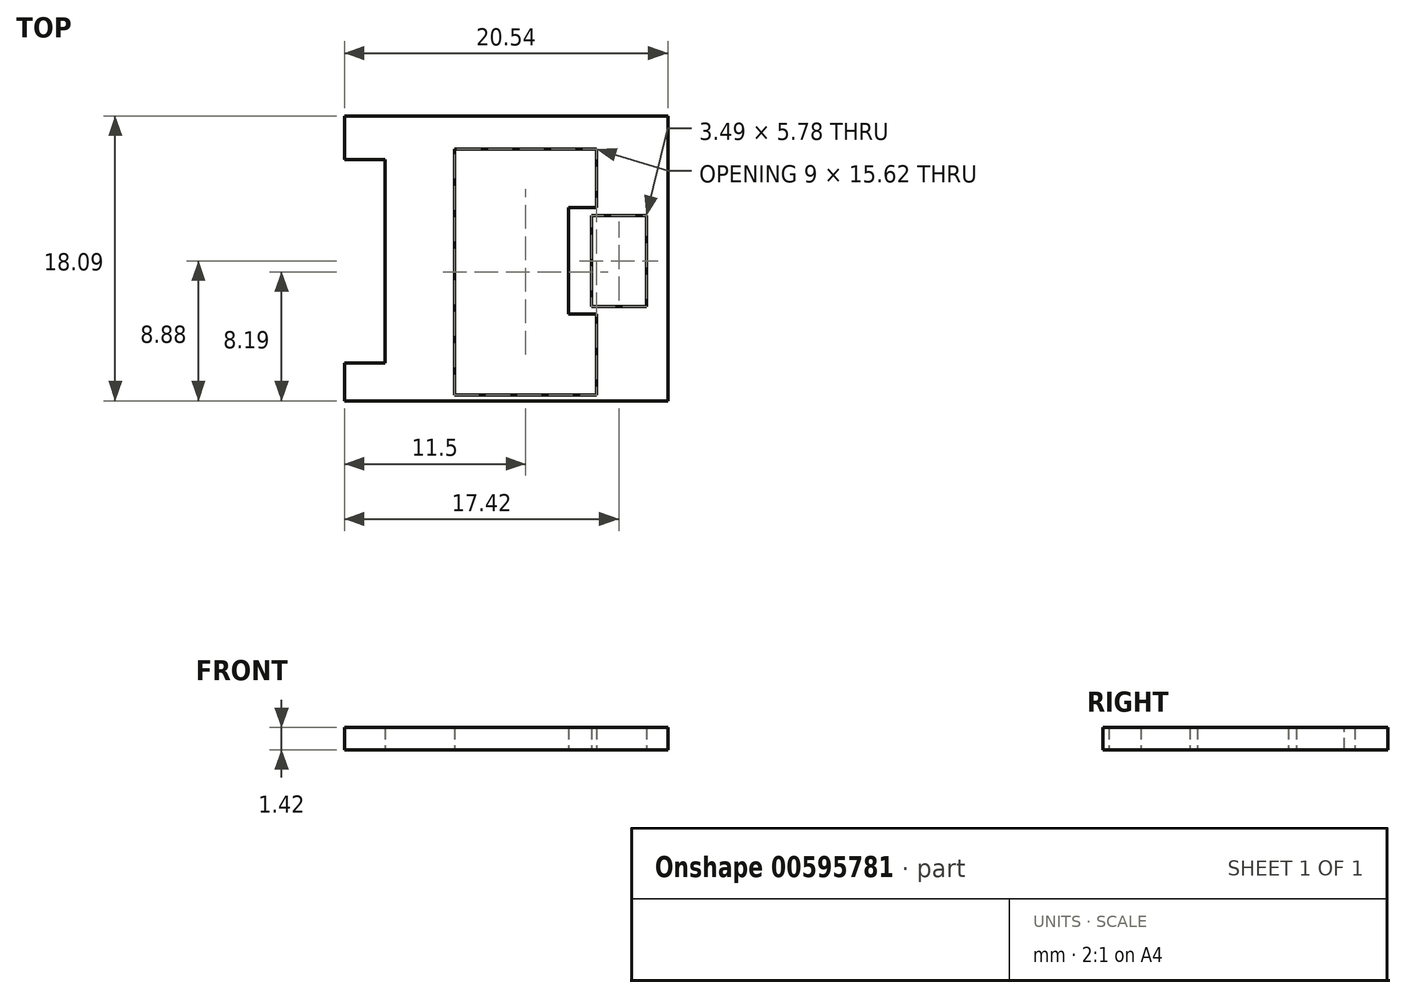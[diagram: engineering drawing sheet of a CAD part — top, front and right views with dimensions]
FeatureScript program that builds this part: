
annotation { "Feature Type Name" : "Feature", "Feature Type Description" : "" }
export const myFeature = defineFeature(function(context is Context, id is Id, definition is map)
    precondition{}
    {
        {
            var Q0;
            Q0=qCreatedBy(makeId("Top.planeOp"),FACE);
            var sketch = newSketch(context, id + "F0", { "sketchPlane" : qUnion([Q0])});
            skLineSegment(sketch, "E0.bottom", {"start": v(0, 0) * mm, "end": v(20.54, 0) * mm});
            skLineSegment(sketch, "E0.top", {"start": v(0, 18.1) * mm, "end": v(20.54, 18.1) * mm});
            skLineSegment(sketch, "E0.left", {"start": v(0, 0) * mm, "end": v(0, 18.1) * mm});
            skLineSegment(sketch, "E0.right", {"start": v(20.54, 0) * mm, "end": v(20.54, 18.1) * mm});
            skLineSegment(sketch, "E1.bottom", {"start": v(2.58, 15.3) * mm, "end": v(0.01, 15.3) * mm});
            skLineSegment(sketch, "E1.top", {"start": v(2.58, 2.4) * mm, "end": v(0.01, 2.4) * mm});
            skLineSegment(sketch, "E1.left", {"start": v(2.59, 15.3) * mm, "end": v(2.59, 2.4) * mm});
            skLineSegment(sketch, "E1.right", {"start": v(0.02, 15.3) * mm, "end": v(0.02, 2.4) * mm});
            skPoint(sketch, "E1.middle", {"position": v(1.3, 8.86) * mm});
            skLineSegment(sketch, "E2", {"start": v(7, 16) * mm, "end": v(16, 16) * mm});
            skLineSegment(sketch, "E3", {"start": v(16, 16) * mm, "end": v(16, 12.27) * mm});
            skLineSegment(sketch, "E4", {"start": v(16, 12.27) * mm, "end": v(14.23, 12.27) * mm});
            skLineSegment(sketch, "E5", {"start": v(14.23, 12.27) * mm, "end": v(14.23, 5.5) * mm});
            skLineSegment(sketch, "E6", {"start": v(14.23, 5.5) * mm, "end": v(16, 5.5) * mm});
            skLineSegment(sketch, "E7", {"start": v(16, 5.5) * mm, "end": v(16, 0.38) * mm});
            skLineSegment(sketch, "E8", {"start": v(16, 0.38) * mm, "end": v(7, 0.38) * mm});
            skLineSegment(sketch, "E9", {"start": v(7, 0.38) * mm, "end": v(7, 16) * mm});
            skLineSegment(sketch, "E10.bottom", {"start": v(19.17, 11.77) * mm, "end": v(15.68, 11.77) * mm});
            skLineSegment(sketch, "E10.top", {"start": v(19.17, 6) * mm, "end": v(15.68, 6) * mm});
            skLineSegment(sketch, "E10.left", {"start": v(19.17, 11.77) * mm, "end": v(19.17, 6) * mm});
            skLineSegment(sketch, "E10.right", {"start": v(15.68, 11.77) * mm, "end": v(15.68, 6) * mm});
            skPoint(sketch, "E10.middle", {"position": v(17.42, 8.88) * mm});
            skSolve(sketch);
        }
        {
            var Q0;
            Q0=makeQuery(id+"F0.imprint","IMPRINT",FACE,{"disambiguationData":[TD([[makeQuery(id+"F0.imprint","IMPRINT",EDGE,{"derivedFrom":sQuery(id+"F0.wireOp",EDGE,"E0.bottom")}),1.0]])]});
            extrude(context, id + "F1", {"entities" : qUnion([Q0]), "depth" : 1.42 * mm, "offsetDistance" : 25 * mm});
        }
        {
            var Q0;
            Q0=makeQuery(id+"F1.opExtrude","CAP_FACE",FACE,{"disambiguationData":[OSD([sQuery(id+"F0.wireOp",EDGE,"E0.bottom"),sQuery(id+"F0.wireOp",EDGE,"E0.top"),sQuery(id+"F0.wireOp",EDGE,"E0.left"),sQuery(id+"F0.wireOp",EDGE,"E0.right"),sQuery(id+"F0.wireOp",EDGE,"E1.bottom"),sQuery(id+"F0.wireOp",EDGE,"E1.top"),sQuery(id+"F0.wireOp",EDGE,"E1.left"),sQuery(id+"F0.wireOp",EDGE,"E1.right"),sQuery(id+"F0.wireOp",EDGE,"E2"),sQuery(id+"F0.wireOp",EDGE,"E3"),sQuery(id+"F0.wireOp",EDGE,"E4"),sQuery(id+"F0.wireOp",EDGE,"E5"),sQuery(id+"F0.wireOp",EDGE,"E6"),sQuery(id+"F0.wireOp",EDGE,"E7"),sQuery(id+"F0.wireOp",EDGE,"E8"),sQuery(id+"F0.wireOp",EDGE,"E9"),sQuery(id+"F0.wireOp",EDGE,"E10.bottom"),sQuery(id+"F0.wireOp",EDGE,"E10.top"),sQuery(id+"F0.wireOp",EDGE,"E10.left"),sQuery(id+"F0.wireOp",EDGE,"E10.right")])],"isStart":false});
            var sketch = newSketch(context, id + "F2", { "sketchPlane" : qUnion([Q0])});
            skLineSegment(sketch, "E11.bottom", {"start": v(0.01, 15.3) * mm, "end": v(0, 15.3) * mm});
            skLineSegment(sketch, "E11.top", {"start": v(0.01, 2.4) * mm, "end": v(0, 2.4) * mm});
            skLineSegment(sketch, "E11.left", {"start": v(0.01, 15.3) * mm, "end": v(0.01, 2.4) * mm});
            skLineSegment(sketch, "E11.right", {"start": v(0, 15.3) * mm, "end": v(0, 2.4) * mm});
            skSolve(sketch);
        }
        {
            var Q0;
            Q0=makeQuery(id+"F2.imprint","IMPRINT",FACE,{"disambiguationData":[TD([[makeQuery(id+"F2.imprint","IMPRINT",EDGE,{"derivedFrom":sQuery(id+"F2.wireOp",EDGE,"E11.bottom")}),1.0]])]});
            extrude(context, id + "F3", {"entities" : qUnion([Q0]), "operationType" : NewBodyOperationType.REMOVE, "endBound" : BoundingType.THROUGH_ALL, "oppositeDirection" : true, "depth" : 25 * mm, "offsetDistance" : 25 * mm});
        }
    });
